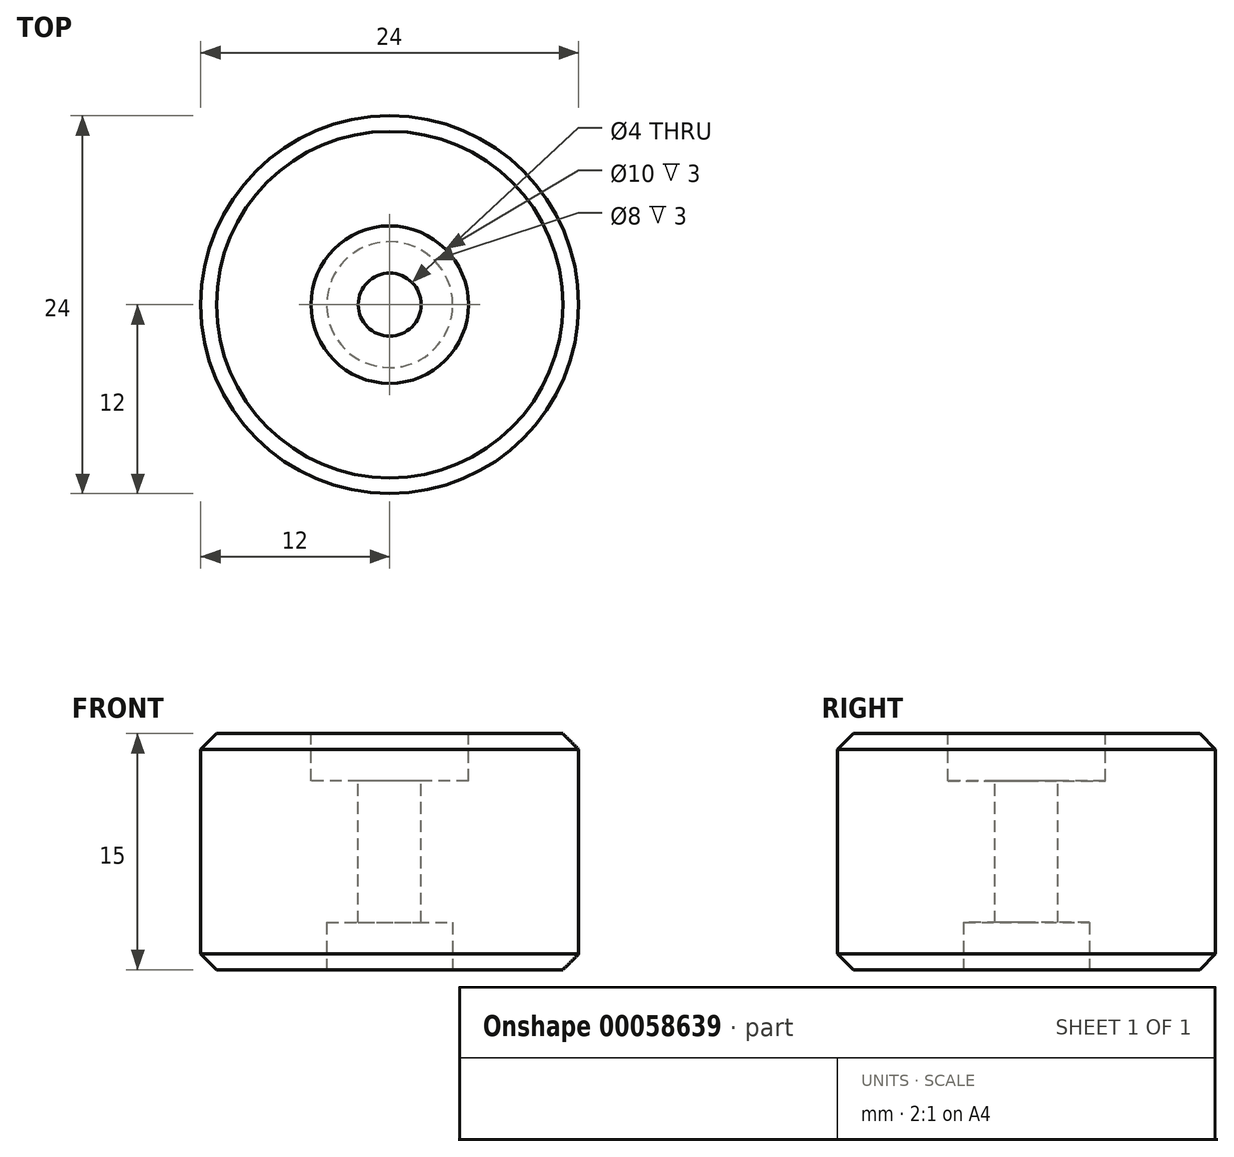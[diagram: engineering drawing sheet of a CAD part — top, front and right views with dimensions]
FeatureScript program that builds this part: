
annotation { "Feature Type Name" : "Feature", "Feature Type Description" : "" }
export const myFeature = defineFeature(function(context is Context, id is Id, definition is map)
    precondition{}
    {
        {
            var Q0;
            Q0=qCreatedBy(makeId("Top.planeOp"),FACE);
            var sketch = newSketch(context, id + "F0", { "sketchPlane" : qUnion([Q0])});
            skCircle(sketch, "E0", {"center": v(0, 0) * mm, "radius": 12 * mm});
            skCircle(sketch, "E1", {"center": v(0, 0) * mm, "radius": 2 * mm});
            skSolve(sketch);
        }
        {
            var Q0;
            Q0=qSketchRegion(id+"F0",true);
            extrude(context, id + "F1", {"entities" : qUnion([Q0]), "oppositeDirection" : true, "depth" : 15 * mm});
        }
        {
            var Q0;
            Q0=makeQuery(id+"F1.opExtrude","CAP_EDGE",EDGE,{"disambiguationData":[OSD([sQuery(id+"F0.wireOp",EDGE,"E0")])],"isStart":false});
            var Q1;
            Q1=makeQuery(id+"F1.opExtrude","CAP_EDGE",EDGE,{"disambiguationData":[OSD([sQuery(id+"F0.wireOp",EDGE,"E0")])],"isStart":true});
            chamfer(context, id + "F2", {"entities" : qUnion([Q0, Q1]), "width" : 1 * mm, "tangentPropagation" : true});
        }
        {
            var Q0;
            Q0=makeQuery(id+"F1.opExtrude","CAP_FACE",FACE,{"disambiguationData":[OSD([sQuery(id+"F0.wireOp",EDGE,"E0"),sQuery(id+"F0.wireOp",EDGE,"E1")])],"isStart":true});
            var sketch = newSketch(context, id + "F3", { "sketchPlane" : qUnion([Q0])});
            skCircle(sketch, "E2", {"center": v(0, 0) * mm, "radius": 5 * mm});
            skSolve(sketch);
        }
        {
            var Q0;
            Q0=makeQuery(id+"F3.imprint","IMPRINT",FACE,{"disambiguationData":[TD([[makeQuery(id+"F3.imprint","IMPRINT",EDGE,{"derivedFrom":sQuery(id+"F3.wireOp",EDGE,"E2")}),1.0]])]});
            extrude(context, id + "F4", {"entities" : qUnion([Q0]), "operationType" : NewBodyOperationType.REMOVE, "oppositeDirection" : true, "depth" : 3 * mm});
        }
        {
            var Q0;
            Q0=makeQuery(id+"F1.opExtrude","CAP_FACE",FACE,{"disambiguationData":[OSD([sQuery(id+"F0.wireOp",EDGE,"E0"),sQuery(id+"F0.wireOp",EDGE,"E1")])],"isStart":false});
            var sketch = newSketch(context, id + "F5", { "sketchPlane" : qUnion([Q0])});
            skCircle(sketch, "E3", {"center": v(0, 0) * mm, "radius": 4 * mm});
            skSolve(sketch);
        }
        {
            var Q0;
            Q0=qSketchRegion(id+"F5",true);
            extrude(context, id + "F6", {"entities" : qUnion([Q0]), "operationType" : NewBodyOperationType.REMOVE, "oppositeDirection" : true, "depth" : 3 * mm});
        }
    });
